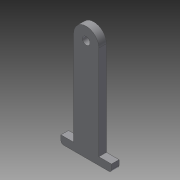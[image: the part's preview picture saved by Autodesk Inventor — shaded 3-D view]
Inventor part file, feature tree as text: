
AUTODESK INVENTOR PART (.ipt)
format: ipt  version: 2015 (Build 190159000, 159)  size: 96,256 bytes
history: native  units: in
note: dims shown in document units (in); Inventor stores cm internally (conversion verified against a paired STEP export)
features: extrude x2, fillet x1, sketch x1
ambient origin geometry x8: Origin, YZ Plane, XZ Plane, XY Plane, X Axis, Y Axis, Z Axis, Center Point
bodies: Solid1 (feature_tree)
feature tree (4):
  extrude  "Extrusion1"  Depth=0.1181in TaperAngle=0.0deg
  extrude  "Extrusion2"  Depth=0.1181in
  fillet  "Fillet1"  Radius=0.1181in
  sketch  "Sketch2"  dims[d2=0.1181in d3=0.1181in d4=0.0in d5=0.1181in d7=0.1181in d8=0.0in d9=0.0394in d13=0.3937in d15=1.4665in d16=0.2362in d17=0.1969in d18=0.1969in]
